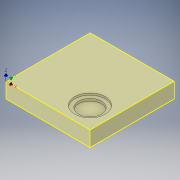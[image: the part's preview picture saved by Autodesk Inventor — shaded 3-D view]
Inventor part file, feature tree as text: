
AUTODESK INVENTOR PART (.ipt)
format: ipt  version: 2017 SP1 (Build 210196100, 196)  size: 218,624 bytes
history: native  units: in
note: dims shown in document units (in); Inventor stores cm internally (conversion verified against a paired STEP export)
features: extrude x3, sketch x3, projected_geometry x1
ambient origin geometry x8: Origin, YZ Plane, XZ Plane, XY Plane, X Axis, Y Axis, Z Axis, Center Point
bodies: Solid1 (feature_tree)
feature tree (7):
  extrude  "Extrusion1"  Depth=5.5in
  extrude  "Extrusion2"  Depth=1.0in
  extrude  "Extrusion3"  Depth=0.155in
  sketch  "Sketch1"  dims[d0=5.5in d1=5.5in]
  sketch  "Sketch2"  dims[d2=1.0in d3=0.0in d4=2.0in]
  projected_geometry  "Projected Loop1"
  sketch  "Sketch3"  dims[d5=1.375in d6=1.375in d7=0.125in d8=0.0in d9=1.5in d10=0.155in d11=0.0in]
